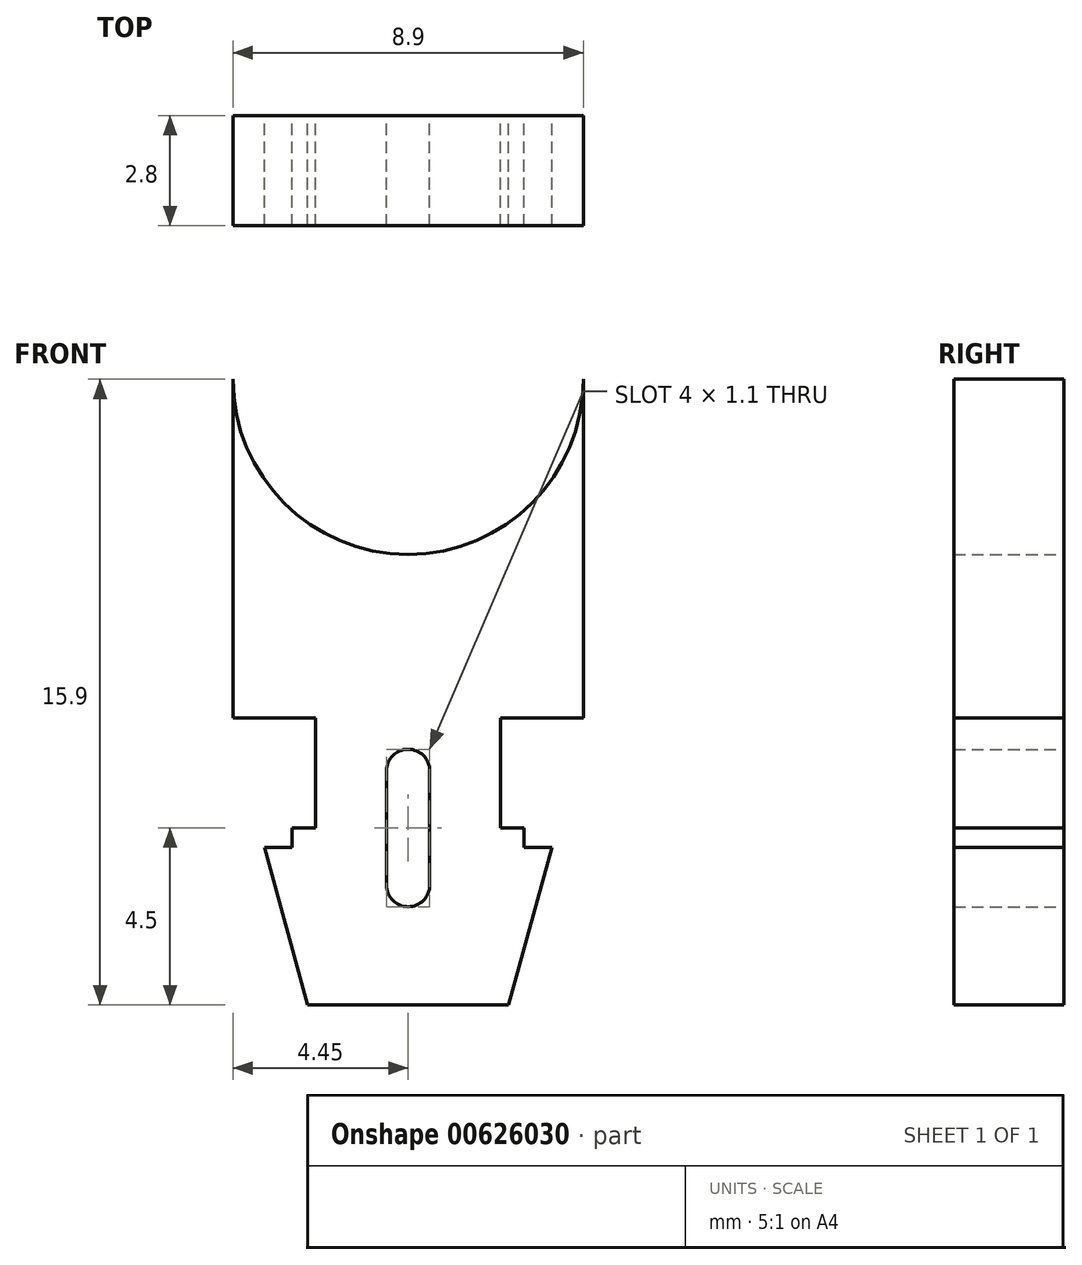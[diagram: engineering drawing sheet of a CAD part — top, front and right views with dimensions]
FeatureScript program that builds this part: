
annotation { "Feature Type Name" : "Feature", "Feature Type Description" : "" }
export const myFeature = defineFeature(function(context is Context, id is Id, definition is map)
    precondition{}
    {
        {
            var Q0;
            Q0=qCreatedBy(makeId("Front.planeOp"),FACE);
            var sketch = newSketch(context, id + "F0", { "sketchPlane" : qUnion([Q0])});
            skArc(sketch, "E0", {"start": v(-4.45, 11.4) * mm, "mid": v(0, 6.95) * mm, "end": v(4.45, 11.4) * mm});
            skPoint(sketch, "E1", {"position": v(-4.45, 11.4) * mm});
            skPoint(sketch, "E2", {"position": v(4.45, 11.4) * mm});
            skLineSegment(sketch, "E3", {"start": v(-4.45, 11.4) * mm, "end": v(-4.45, 2.8) * mm});
            skLineSegment(sketch, "E4", {"start": v(4.45, 11.4) * mm, "end": v(4.45, 2.8) * mm});
            skLineSegment(sketch, "E5", {"start": v(-4.45, 2.8) * mm, "end": v(-2.35, 2.8) * mm});
            skLineSegment(sketch, "E6", {"start": v(-2.35, 2.8) * mm, "end": v(-2.35, 0) * mm});
            skLineSegment(sketch, "E7", {"start": v(4.45, 2.8) * mm, "end": v(2.35, 2.8) * mm});
            skLineSegment(sketch, "E8", {"start": v(2.35, 2.8) * mm, "end": v(2.35, 0) * mm});
            skLineSegment(sketch, "E9", {"start": v(2.35, 0) * mm, "end": v(2.95, 0) * mm});
            skLineSegment(sketch, "E10", {"start": v(-2.35, 0) * mm, "end": v(-2.95, 0) * mm});
            skLineSegment(sketch, "E11", {"start": v(-2.95, 0) * mm, "end": v(-2.95, -0.5) * mm});
            skLineSegment(sketch, "E12", {"start": v(2.95, 0) * mm, "end": v(2.95, -0.5) * mm});
            skLineSegment(sketch, "E13", {"start": v(2.95, -0.5) * mm, "end": v(3.65, -0.5) * mm});
            skLineSegment(sketch, "E14", {"start": v(-2.95, -0.5) * mm, "end": v(-3.65, -0.5) * mm});
            skLineSegment(sketch, "E15", {"start": v(-3.65, -0.5) * mm, "end": v(-2.55, -4.5) * mm});
            skLineSegment(sketch, "E16", {"start": v(2.55, -4.5) * mm, "end": v(3.65, -0.5) * mm});
            skLineSegment(sketch, "E17", {"start": v(-2.55, -4.5) * mm, "end": v(2.55, -4.5) * mm});
            skPoint(sketch, "E18.orphan", {"position": v(0, -13.77) * mm});
            skLineSegment(sketch, "E19.bottom", {"start": v(0, 0) * mm, "end": v(0, 0) * mm});
            skLineSegment(sketch, "E20.left", {"start": v(0.55, 1.45) * mm, "end": v(0.55, -1.45) * mm});
            skLineSegment(sketch, "E20.right", {"start": v(-0.55, 1.45) * mm, "end": v(-0.55, -1.45) * mm});
            skPoint(sketch, "E20.middle", {"position": v(0, 0) * mm});
            skArc(sketch, "E21", {"start": v(0.55, -1.45) * mm, "mid": v(0, -2) * mm, "end": v(-0.55, -1.45) * mm});
            skArc(sketch, "E22", {"start": v(-0.55, 1.45) * mm, "mid": v(0, 2) * mm, "end": v(0.55, 1.45) * mm});
            skPoint(sketch, "E23", {"position": v(0, 2) * mm});
            skPoint(sketch, "E24", {"position": v(0, -2) * mm});
            skSolve(sketch);
        }
        {
            var Q0;
            Q0 = qSketchRegion(id + "F0", true);
            extrude(context, id + "F1", {"entities" : qUnion([Q0]), "depth" : 2.8 * mm, "offsetDistance" : 25 * mm});
        }
    });
